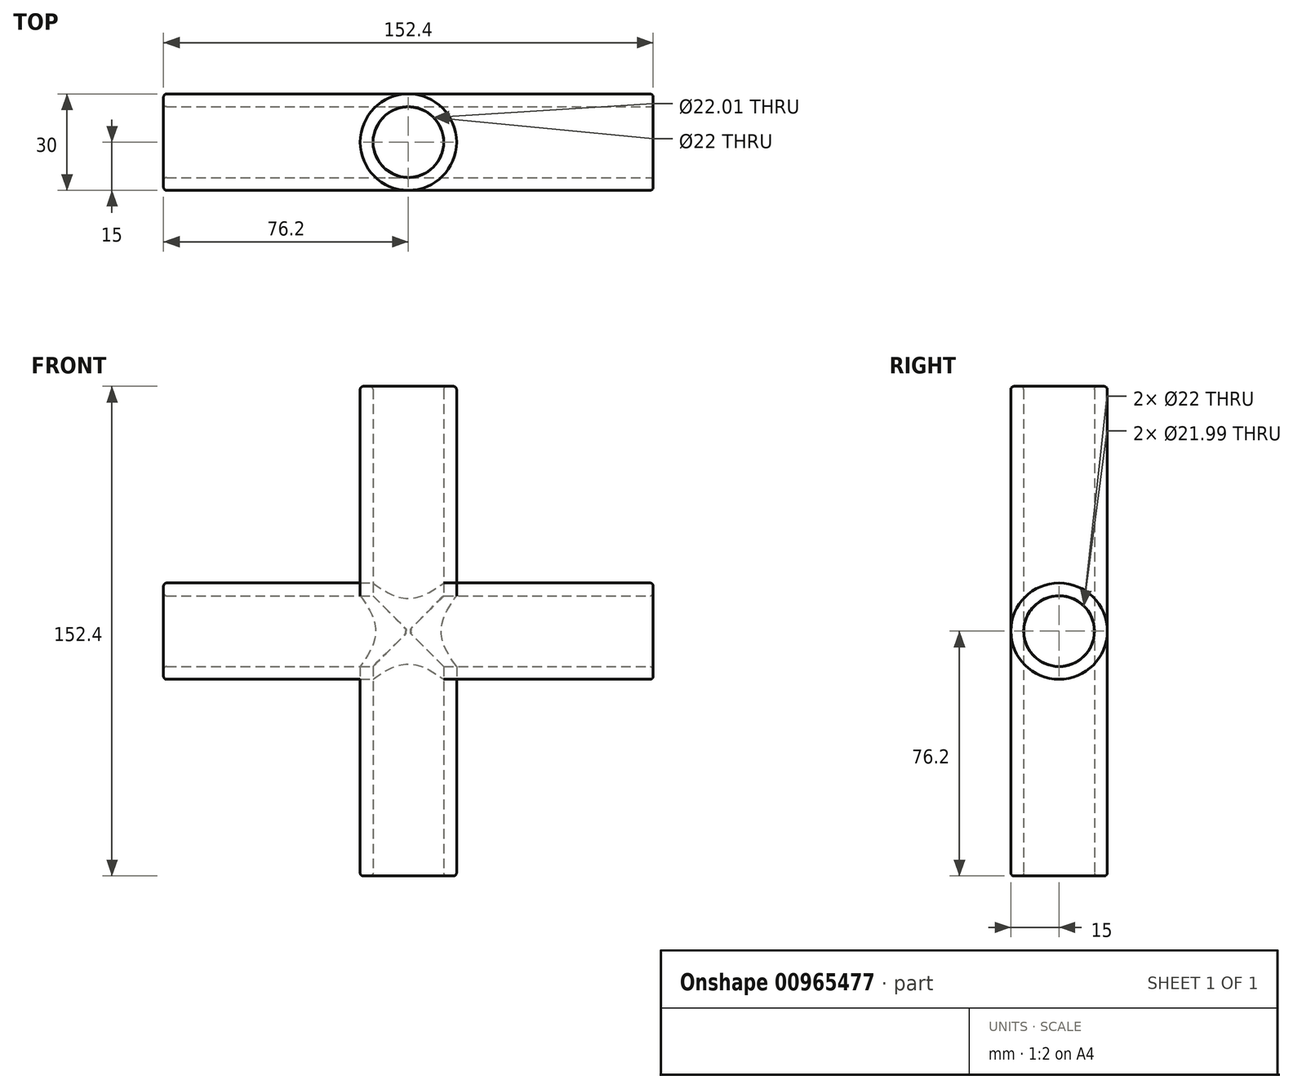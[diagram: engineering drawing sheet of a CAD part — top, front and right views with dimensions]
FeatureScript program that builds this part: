
annotation { "Feature Type Name" : "Feature", "Feature Type Description" : "" }
export const myFeature = defineFeature(function(context is Context, id is Id, definition is map)
    precondition{}
    {
        {
            var Q0;
            Q0=qCreatedBy(makeId("Top.planeOp"),FACE);
            var sketch = newSketch(context, id + "F0", { "sketchPlane" : qUnion([Q0])});
            skCircle(sketch, "E0", {"center": v(0, 0) * mm, "radius": 15 * mm});
            skCircle(sketch, "E1", {"center": v(0, 0) * mm, "radius": 11 * mm});
            skSolve(sketch);
        }
        {
            var Q0;
            Q0 = qSketchRegion(id + "F0", true);
            extrude(context, id + "F1", {"entities" : qUnion([Q0]), "endBound" : BoundingType.SYMMETRIC, "depth" : 152.4 * mm, "offsetDistance" : 25.4 * mm});
        }
        {
            var Q0;
            Q0=qCreatedBy(makeId("Right.planeOp"),FACE);
            var sketch = newSketch(context, id + "F2", { "sketchPlane" : qUnion([Q0])});
            skLineSegment(sketch, "E2", {"start": v(43.57, 0) * mm, "end": v(-50.69, 0) * mm, "construction": true});
            skSolve(sketch);
        }
        {
            var Q0;
            Q0=makeQuery(id+"F1.opExtrude","SWEPT_BODY",BODY,{"disambiguationData":[OSD([sQuery(id+"F0.wireOp",EDGE,"E0"),sQuery(id+"F0.wireOp",EDGE,"E1")])]});
            var Q1;
            Q1=sQuery(id+"F2.wireOp",EDGE,"E2");
            circularPattern(context, id + "F3", {"entities" : qUnion([Q0]), "axis" : qUnion([Q1]), "angle" : 90 * degree, "instanceCount" : 2, "equalSpace" : true});
        }
        {
            var Q0;
            Q0=makeQuery(id+"F3.opPattern","COPY",FACE,{"derivedFrom":makeQuery(id+"F1.opExtrude","CAP_FACE",FACE,{"disambiguationData":[OSD([sQuery(id+"F0.wireOp",EDGE,"E0"),sQuery(id+"F0.wireOp",EDGE,"E1")])],"isStart":true}),"instanceName":"1"});
            var sketch = newSketch(context, id + "F4", { "sketchPlane" : qUnion([Q0])});
            skCircle(sketch, "E3", {"center": v(0, 0) * mm, "radius": 11 * mm});
            skSolve(sketch);
        }
        {
            var Q0;
            Q0=makeQuery(id+"F1.opExtrude","CAP_EDGE",EDGE,{"disambiguationData":[OSD([sQuery(id+"F0.wireOp",EDGE,"E1")])],"isStart":false});
            var Q1;
            Q1=makeQuery(id+"F1.opExtrude","CAP_EDGE",EDGE,{"disambiguationData":[OSD([sQuery(id+"F0.wireOp",EDGE,"E0")])],"isStart":false});
            var Q2;
            Q2=makeQuery(id+"F3.opPattern","COPY",EDGE,{"derivedFrom":makeQuery(id+"F1.opExtrude","CAP_EDGE",EDGE,{"disambiguationData":[OSD([sQuery(id+"F0.wireOp",EDGE,"E0")])],"isStart":false}),"instanceName":"3"});
            var Q3;
            Q3=makeQuery(id+"F3.opPattern","COPY",EDGE,{"derivedFrom":makeQuery(id+"F1.opExtrude","CAP_EDGE",EDGE,{"disambiguationData":[OSD([sQuery(id+"F0.wireOp",EDGE,"E1")])],"isStart":false}),"instanceName":"3"});
            var Q4;
            Q4=makeQuery(id+"F3.opPattern","COPY",EDGE,{"derivedFrom":makeQuery(id+"F1.opExtrude","CAP_EDGE",EDGE,{"disambiguationData":[OSD([sQuery(id+"F0.wireOp",EDGE,"E0")])],"isStart":false}),"instanceName":"2"});
            var Q5;
            Q5=makeQuery(id+"F3.opPattern","COPY",EDGE,{"derivedFrom":makeQuery(id+"F1.opExtrude","CAP_EDGE",EDGE,{"disambiguationData":[OSD([sQuery(id+"F0.wireOp",EDGE,"E1")])],"isStart":false}),"instanceName":"2"});
            var Q6;
            Q6=makeQuery(id+"F3.opPattern","COPY",EDGE,{"derivedFrom":makeQuery(id+"F1.opExtrude","CAP_EDGE",EDGE,{"disambiguationData":[OSD([sQuery(id+"F0.wireOp",EDGE,"E1")])],"isStart":false}),"instanceName":"1"});
            var Q7;
            Q7=makeQuery(id+"F3.opPattern","COPY",EDGE,{"derivedFrom":makeQuery(id+"F1.opExtrude","CAP_EDGE",EDGE,{"disambiguationData":[OSD([sQuery(id+"F0.wireOp",EDGE,"E0")])],"isStart":false}),"instanceName":"1"});
            var Q8;
            Q8=makeQuery(id+"F1.opExtrude","CAP_EDGE",EDGE,{"disambiguationData":[OSD([sQuery(id+"F0.wireOp",EDGE,"E0")])],"isStart":true});
            var Q9;
            Q9=makeQuery(id+"F1.opExtrude","CAP_EDGE",EDGE,{"disambiguationData":[OSD([sQuery(id+"F0.wireOp",EDGE,"E1")])],"isStart":true});
            var Q10;
            Q10=makeQuery(id+"F3.opPattern","COPY",EDGE,{"derivedFrom":makeQuery(id+"F1.opExtrude","CAP_EDGE",EDGE,{"disambiguationData":[OSD([sQuery(id+"F0.wireOp",EDGE,"E1")])],"isStart":true}),"instanceName":"1"});
            var Q11;
            Q11=makeQuery(id+"F3.opPattern","COPY",EDGE,{"derivedFrom":makeQuery(id+"F1.opExtrude","CAP_EDGE",EDGE,{"disambiguationData":[OSD([sQuery(id+"F0.wireOp",EDGE,"E0")])],"isStart":true}),"instanceName":"1"});
            fillet(context, id + "F5", {"entities" : qUnion([Q0, Q1, Q2, Q3, Q4, Q5, Q6, Q7, Q8, Q9, Q10, Q11]), "radius" : 1 * mm, "tangentPropagation" : true, "allowEdgeOverflow" : false});
        }
        {
            var Q0;
            Q0=makeQuery(id+"F4.imprint","IMPRINT",FACE,{"disambiguationData":[TD([[makeQuery(id+"F4.imprint","IMPRINT",EDGE,{"derivedFrom":sQuery(id+"F4.wireOp",EDGE,"E3")}),1.0]])]});
            extrude(context, id + "F6", {"entities" : qUnion([Q0]), "operationType" : NewBodyOperationType.REMOVE, "oppositeDirection" : true, "depth" : 146.05 * mm, "offsetDistance" : 25.4 * mm});
        }
        {
            var Q0;
            Q0=makeQuery(id+"F1.opExtrude","CAP_FACE",FACE,{"disambiguationData":[OSD([sQuery(id+"F0.wireOp",EDGE,"E0"),sQuery(id+"F0.wireOp",EDGE,"E1")])],"isStart":true});
            var sketch = newSketch(context, id + "F7", { "sketchPlane" : qUnion([Q0])});
            skCircle(sketch, "E4", {"center": v(0, 0) * mm, "radius": 11 * mm});
            skSolve(sketch);
        }
        {
            var Q0;
            Q0 = qSketchRegion(id + "F7", true);
            extrude(context, id + "F8", {"entities" : qUnion([Q0]), "operationType" : NewBodyOperationType.REMOVE, "oppositeDirection" : true, "depth" : 104.14 * mm, "offsetDistance" : 25.4 * mm});
        }
    });
